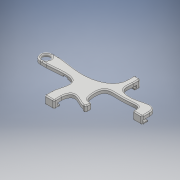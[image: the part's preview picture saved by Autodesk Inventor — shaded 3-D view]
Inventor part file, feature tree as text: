
AUTODESK INVENTOR PART (.ipt)
format: ipt  version: 2018 (Build 220112000, 112)  size: 464,896 bytes
history: native  units: mm
features: fillet x6, extrude x5, sketch x5, reference x2, other x2
ambient origin geometry x8: Origin, YZ Plane, XZ Plane, XY Plane, X Axis, Y Axis, Z Axis, Center Point
bodies: Solid1 (feature_tree)
feature tree (20):
  extrude  "Extrusion1"  Depth=6.0mm
  extrude  "Extrusion2"  Depth=3.0mm
  extrude  "Extrusion3"  Depth=3.0mm
  fillet  "Fillet1"  [1 undecoded]
  fillet  "Fillet2"  Radius=5.0mm
  fillet  "Fillet3"  Radius=6.0mm
  fillet  "Fillet4"  Radius=8.0mm
  extrude  "Extrusion4"  Depth=10.0mm
  extrude  "Extrusion5"  Depth=0.8mm
  fillet  "Fillet5"  Radius=14.0mm
  fillet  "Fillet6"  Radius=15.0mm
  sketch  "Sketch1"  dims[d0=20.0mm d1=6.0mm]
  reference  "Reference1"
  sketch  "Sketch2"  dims[d2=4.0mm d3=3.0mm]
  sketch  "Sketch3"  dims[d4=3.0mm d5=3.0mm d6=0.0mm d7=5.0mm d8=6.0mm d9=8.0mm]
  sketch  "Sketch4"  dims[d10=6.0mm d11=10.0mm]
  reference  "Reference2"
  sketch  "Sketch5"  dims[d12=2.0mm d13=5.0mm d14=14.0mm d15=15.0mm d16=6.0mm d17=8.0mm d18=5.0mm d19=10.0mm d20=6.0mm d21=5.0mm d22=3.0mm d23=0.0mm d24=8.0mm d25=3.0mm d26=8.0mm d27=3.0mm d28=5.0mm d29=3.0mm d30=2.0mm d31=5.0mm d32=2.0mm d33=0.0mm d34=8.0mm d35=4.5mm d36=5.0mm d37=4.5mm d38=8.0mm d39=4.5mm d40=1.5mm d41=0.0mm d42=4.0mm d43=1.2mm d44=0.8mm d45=0.8mm d46=7.0mm d47=15.0mm d48=4.0mm d49=10.0mm d50=1.0mm d51=0.0mm d52=0.0mm d53=4.0mm d54=3.0mm d55=4.0mm d56=10.0mm d57=10.0mm d58=5.0mm d59=6.0mm d60=1.0mm d61=0.0mm d62=1.5mm d63=0.8mm]
  other  "Assembly1"
  other  "PCB:1"
note: 1 required parameter value undecoded (feature->parameter linkage not recoverable at this tier; creation-order binding heuristic only, values carry confidence <= 0.55)
